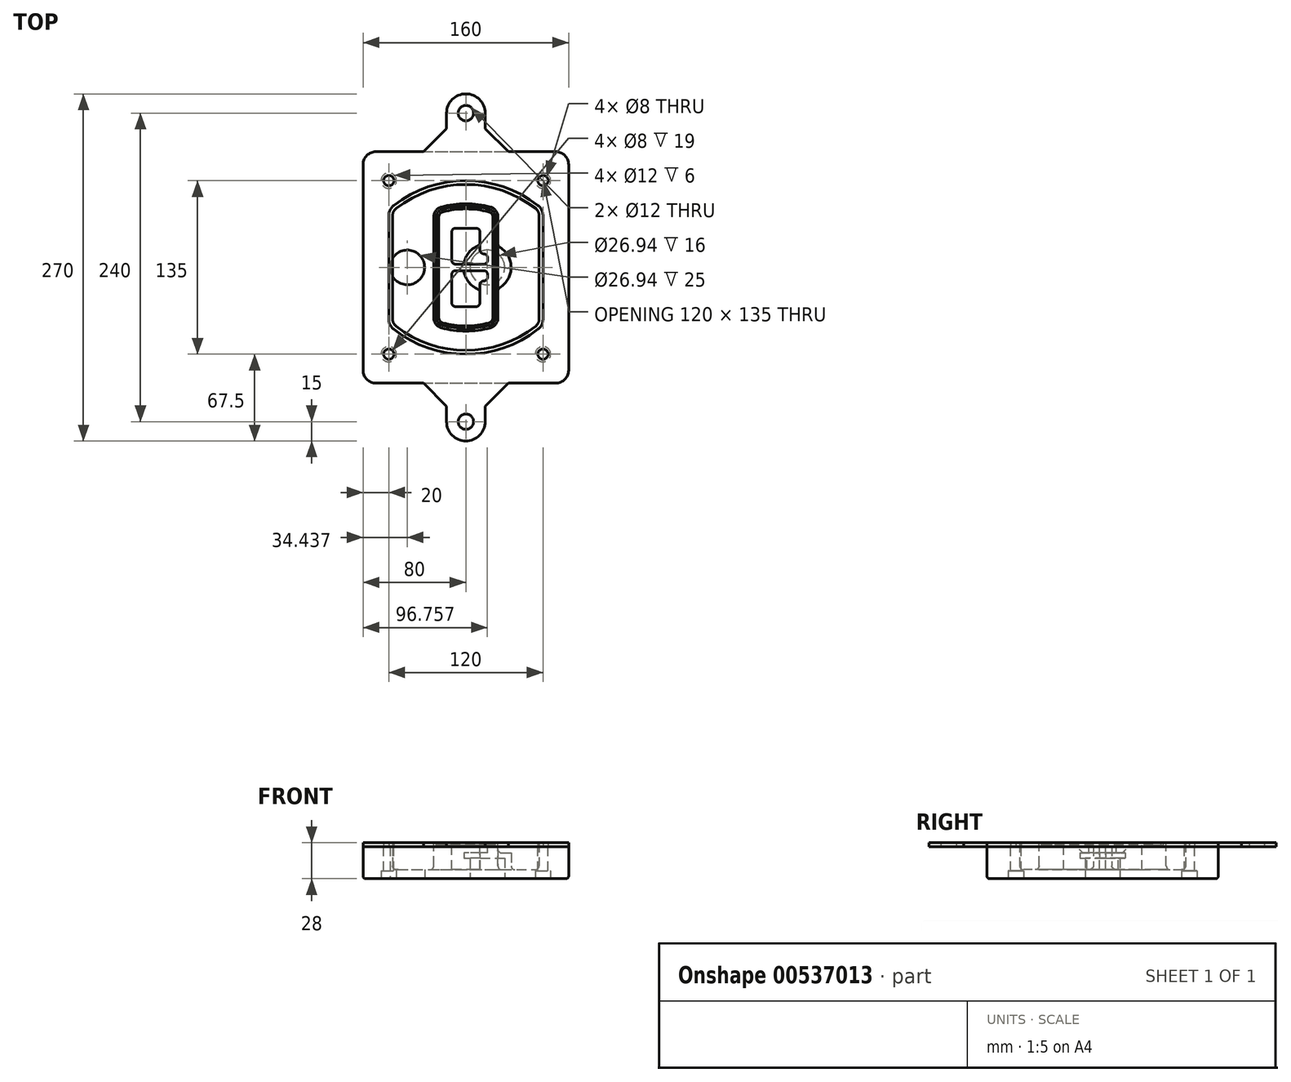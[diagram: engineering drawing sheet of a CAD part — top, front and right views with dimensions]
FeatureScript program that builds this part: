
annotation { "Feature Type Name" : "Feature", "Feature Type Description" : "" }
export const myFeature = defineFeature(function(context is Context, id is Id, definition is map)
    precondition{}
    {
        {
            var Q0;
            Q0=qCreatedBy(makeId("Top.planeOp"),FACE);
            var sketch = newSketch(context, id + "F0", { "sketchPlane" : qUnion([Q0])});
            skPoint(sketch, "E0.rect.middle", {"position": v(0, 0) * mm});
            skLineSegment(sketch, "E1.bottom", {"start": v(-70, -90) * mm, "end": v(70, -90) * mm});
            skLineSegment(sketch, "E1.top", {"start": v(-70, 90) * mm, "end": v(70, 90) * mm});
            skLineSegment(sketch, "E1.left", {"start": v(-80, -80) * mm, "end": v(-80, 80) * mm});
            skLineSegment(sketch, "E1.right", {"start": v(80, -80) * mm, "end": v(80, 80) * mm});
            skLineSegment(sketch, "E2", {"start": v(-80, 90) * mm, "end": v(80, -90) * mm, "construction": true});
            skLineSegment(sketch, "E3", {"start": v(80, 90) * mm, "end": v(-80, -90) * mm, "construction": true});
            skCircle(sketch, "E4", {"center": v(-60, 67.5) * mm, "radius": 4 * mm});
            skCircle(sketch, "E5", {"center": v(60, 67.5) * mm, "radius": 4 * mm});
            skCircle(sketch, "E6", {"center": v(60, -67.5) * mm, "radius": 4 * mm});
            skCircle(sketch, "E7", {"center": v(-60, -67.5) * mm, "radius": 4 * mm});
            skLineSegment(sketch, "E8", {"start": v(-60, 67.5) * mm, "end": v(60, 67.5) * mm, "construction": true});
            skLineSegment(sketch, "E9", {"start": v(60, 67.5) * mm, "end": v(60, -67.5) * mm, "construction": true});
            skLineSegment(sketch, "E10", {"start": v(60, -67.5) * mm, "end": v(-60, -67.5) * mm, "construction": true});
            skLineSegment(sketch, "E11", {"start": v(-60, -67.5) * mm, "end": v(-60, 67.5) * mm, "construction": true});
            skLineSegment(sketch, "E12", {"start": v(-60, 40.3) * mm, "end": v(-60, -40.3) * mm});
            skLineSegment(sketch, "E13", {"start": v(60, 40.3) * mm, "end": v(60, -40.3) * mm});
            skArc(sketch, "E14", {"start": v(56.15, 48.18) * mm, "mid": v(0, 67.5) * mm, "end": v(-56.15, 48.18) * mm});
            skArc(sketch, "E15", {"start": v(-56.15, -48.18) * mm, "mid": v(0, -67.5) * mm, "end": v(56.15, -48.18) * mm});
            skLineSegment(sketch, "E16", {"start": v(-60, 0) * mm, "end": v(60, 0) * mm, "construction": true});
            skPoint(sketch, "E17.visualSharp", {"position": v(-60, -45) * mm});
            skArc(sketch, "E17.filletArc", {"start": v(-60, -40.3) * mm, "mid": v(-58.99, -44.68) * mm, "end": v(-56.15, -48.18) * mm});
            skPoint(sketch, "E18.visualSharp", {"position": v(-60, 45) * mm});
            skArc(sketch, "E18.filletArc", {"start": v(-56.15, 48.18) * mm, "mid": v(-58.99, 44.68) * mm, "end": v(-60, 40.3) * mm});
            skPoint(sketch, "E19.visualSharp", {"position": v(60, 45) * mm});
            skArc(sketch, "E19.filletArc", {"start": v(60, 40.3) * mm, "mid": v(58.99, 44.68) * mm, "end": v(56.15, 48.18) * mm});
            skPoint(sketch, "E20.visualSharp", {"position": v(60, -45) * mm});
            skArc(sketch, "E20.filletArc", {"start": v(56.15, -48.18) * mm, "mid": v(58.99, -44.68) * mm, "end": v(60, -40.3) * mm});
            skPoint(sketch, "E21.visualSharp", {"position": v(-80, 90) * mm});
            skArc(sketch, "E21.filletArc", {"start": v(-70, 90) * mm, "mid": v(-77.07, 87.07) * mm, "end": v(-80, 80) * mm});
            skPoint(sketch, "E22.visualSharp", {"position": v(80, 90) * mm});
            skArc(sketch, "E22.filletArc", {"start": v(80, 80) * mm, "mid": v(77.07, 87.07) * mm, "end": v(70, 90) * mm});
            skPoint(sketch, "E23.visualSharp", {"position": v(80, -90) * mm});
            skArc(sketch, "E23.filletArc", {"start": v(70, -90) * mm, "mid": v(77.07, -87.07) * mm, "end": v(80, -80) * mm});
            skPoint(sketch, "E24.visualSharp", {"position": v(-80, -90) * mm});
            skArc(sketch, "E24.filletArc", {"start": v(-80, -80) * mm, "mid": v(-77.07, -87.07) * mm, "end": v(-70, -90) * mm});
            skArc(sketch, "E25.0", {"start": v(57, 40.3) * mm, "mid": v(56.3, 43.36) * mm, "end": v(54.3, 45.81) * mm});
            skLineSegment(sketch, "E25.1", {"start": v(57, 40.3) * mm, "end": v(57, -40.3) * mm});
            skArc(sketch, "E25.2", {"start": v(54.3, -45.81) * mm, "mid": v(56.3, -43.36) * mm, "end": v(57, -40.3) * mm});
            skArc(sketch, "E25.3", {"start": v(-54.3, -45.81) * mm, "mid": v(0, -64.5) * mm, "end": v(54.3, -45.81) * mm});
            skArc(sketch, "E25.4", {"start": v(-57, -40.3) * mm, "mid": v(-56.3, -43.36) * mm, "end": v(-54.3, -45.81) * mm});
            skArc(sketch, "E25.5", {"start": v(54.3, 45.81) * mm, "mid": v(0, 64.5) * mm, "end": v(-54.3, 45.81) * mm});
            skLineSegment(sketch, "E25.6", {"start": v(-57, 40.3) * mm, "end": v(-57, -40.3) * mm});
            skArc(sketch, "E25.7", {"start": v(-54.3, 45.81) * mm, "mid": v(-56.3, 43.36) * mm, "end": v(-57, 40.3) * mm});
            skArc(sketch, "E26.0", {"start": v(-58.62, 51.33) * mm, "mid": v(-62.58, 46.43) * mm, "end": v(-64, 40.3) * mm});
            skArc(sketch, "E26.1", {"start": v(58.62, 51.33) * mm, "mid": v(0, 71.5) * mm, "end": v(-58.62, 51.33) * mm});
            skArc(sketch, "E26.2", {"start": v(64, 40.3) * mm, "mid": v(62.58, 46.43) * mm, "end": v(58.62, 51.33) * mm});
            skLineSegment(sketch, "E26.3", {"start": v(64, 40.3) * mm, "end": v(64, -40.3) * mm});
            skArc(sketch, "E26.4", {"start": v(58.62, -51.33) * mm, "mid": v(62.58, -46.43) * mm, "end": v(64, -40.3) * mm});
            skLineSegment(sketch, "E26.5", {"start": v(-64, 40.3) * mm, "end": v(-64, -40.3) * mm});
            skArc(sketch, "E26.6", {"start": v(-58.62, -51.33) * mm, "mid": v(0, -71.5) * mm, "end": v(58.62, -51.33) * mm});
            skArc(sketch, "E26.7", {"start": v(-64, -40.3) * mm, "mid": v(-62.58, -46.43) * mm, "end": v(-58.62, -51.33) * mm});
            skSolve(sketch);
        }
        {
            var Q0;
            Q0=makeQuery(id+"F0.imprint","IMPRINT",FACE,{"disambiguationData":[TD([[makeQuery(id+"F0.imprint","IMPRINT",EDGE,{"derivedFrom":sQuery(id+"F0.wireOp",EDGE,"E1.bottom")}),1.0]])]});
            var Q1;
            Q1=makeQuery(id+"F0.imprint","IMPRINT",FACE,{"disambiguationData":[TD([[makeQuery(id+"F0.imprint","IMPRINT",EDGE,{"derivedFrom":sQuery(id+"F0.wireOp",EDGE,"E12")}),1.0]])]});
            var Q2;
            Q2=makeQuery(id+"F0.imprint","IMPRINT",FACE,{"disambiguationData":[TD([[makeQuery(id+"F0.imprint","IMPRINT",EDGE,{"derivedFrom":sQuery(id+"F0.wireOp",EDGE,"E25.0")}),1.0]])]});
            var Q3;
            Q3=makeQuery(id+"F0.imprint","IMPRINT",FACE,{"disambiguationData":[TD([[makeQuery(id+"F0.imprint","IMPRINT",EDGE,{"derivedFrom":sQuery(id+"F0.wireOp",EDGE,"E12")}),-1.0]])]});
            extrude(context, id + "F1", {"entities" : qUnion([Q0, Q1, Q2, Q3]), "oppositeDirection" : true, "depth" : 25 * mm});
        }
        {
            var Q0;
            Q0=makeQuery(id+"F0.imprint","IMPRINT",FACE,{"disambiguationData":[TD([[makeQuery(id+"F0.imprint","IMPRINT",EDGE,{"derivedFrom":sQuery(id+"F0.wireOp",EDGE,"E12")}),1.0]])]});
            extrude(context, id + "F2", {"entities" : qUnion([Q0]), "operationType" : NewBodyOperationType.ADD, "depth" : 3 * mm});
        }
        {
            var Q0;
            Q0=makeQuery(id+"F0.imprint","IMPRINT",FACE,{"disambiguationData":[TD([[makeQuery(id+"F0.imprint","IMPRINT",EDGE,{"derivedFrom":sQuery(id+"F0.wireOp",EDGE,"E25.0")}),1.0]])]});
            extrude(context, id + "F3", {"entities" : qUnion([Q0]), "operationType" : NewBodyOperationType.REMOVE, "oppositeDirection" : true, "depth" : 18 * mm});
        }
        {
            var Q0;
            Q0=makeQuery(id+"F2.opExtrude","CAP_FACE",FACE,{"disambiguationData":[OSD([sQuery(id+"F0.wireOp",EDGE,"E12"),sQuery(id+"F0.wireOp",EDGE,"E13"),sQuery(id+"F0.wireOp",EDGE,"E14"),sQuery(id+"F0.wireOp",EDGE,"E15"),sQuery(id+"F0.wireOp",EDGE,"E17.filletArc"),sQuery(id+"F0.wireOp",EDGE,"E18.filletArc"),sQuery(id+"F0.wireOp",EDGE,"E19.filletArc"),sQuery(id+"F0.wireOp",EDGE,"E20.filletArc"),sQuery(id+"F0.wireOp",EDGE,"E25.0"),sQuery(id+"F0.wireOp",EDGE,"E25.1"),sQuery(id+"F0.wireOp",EDGE,"E25.2"),sQuery(id+"F0.wireOp",EDGE,"E25.3"),sQuery(id+"F0.wireOp",EDGE,"E25.4"),sQuery(id+"F0.wireOp",EDGE,"E25.5"),sQuery(id+"F0.wireOp",EDGE,"E25.6"),sQuery(id+"F0.wireOp",EDGE,"E25.7")])],"isStart":false});
            var sketch = newSketch(context, id + "F4", { "sketchPlane" : qUnion([Q0])});
            skArc(sketch, "E27.0", {"start": v(-19.08, -46.97) * mm, "mid": v(0, -49.5) * mm, "end": v(19.08, -46.97) * mm});
            skArc(sketch, "E28.0", {"start": v(19.08, 46.97) * mm, "mid": v(0, 49.5) * mm, "end": v(-19.08, 46.97) * mm});
            skLineSegment(sketch, "E29", {"start": v(-25, 39.25) * mm, "end": v(-25, -39.25) * mm});
            skLineSegment(sketch, "E30", {"start": v(25, 39.25) * mm, "end": v(25, -39.25) * mm});
            skLineSegment(sketch, "E31", {"start": v(-25, 45.1) * mm, "end": v(25, 45.1) * mm, "construction": true});
            skLineSegment(sketch, "E32", {"start": v(-25, -45.1) * mm, "end": v(25, -45.1) * mm, "construction": true});
            skPoint(sketch, "E33.visualSharp", {"position": v(-25, 45.1) * mm});
            skArc(sketch, "E33.filletArc", {"start": v(-19.08, 46.97) * mm, "mid": v(-23.35, 44.11) * mm, "end": v(-25, 39.25) * mm});
            skPoint(sketch, "E34.visualSharp", {"position": v(25, 45.1) * mm});
            skArc(sketch, "E34.filletArc", {"start": v(25, 39.25) * mm, "mid": v(23.35, 44.11) * mm, "end": v(19.08, 46.97) * mm});
            skPoint(sketch, "E35.visualSharp", {"position": v(25, -45.1) * mm});
            skArc(sketch, "E35.filletArc", {"start": v(19.08, -46.97) * mm, "mid": v(23.35, -44.11) * mm, "end": v(25, -39.25) * mm});
            skPoint(sketch, "E36.visualSharp", {"position": v(-25, -45.1) * mm});
            skArc(sketch, "E36.filletArc", {"start": v(-25, -39.25) * mm, "mid": v(-23.35, -44.11) * mm, "end": v(-19.08, -46.97) * mm});
            skArc(sketch, "E37.0", {"start": v(54.3, 45.81) * mm, "mid": v(0, 64.5) * mm, "end": v(-54.3, 45.81) * mm});
            skArc(sketch, "E37.1", {"start": v(-54.3, 45.81) * mm, "mid": v(-56.3, 43.36) * mm, "end": v(-57, 40.3) * mm});
            skLineSegment(sketch, "E37.2", {"start": v(-57, 40.3) * mm, "end": v(-57, -40.3) * mm});
            skArc(sketch, "E37.3", {"start": v(-57, -40.3) * mm, "mid": v(-56.3, -43.36) * mm, "end": v(-54.3, -45.81) * mm});
            skArc(sketch, "E37.4", {"start": v(-54.3, -45.81) * mm, "mid": v(0, -64.5) * mm, "end": v(54.3, -45.81) * mm});
            skArc(sketch, "E37.5", {"start": v(54.3, -45.81) * mm, "mid": v(56.3, -43.36) * mm, "end": v(57, -40.3) * mm});
            skLineSegment(sketch, "E37.6", {"start": v(57, 40.3) * mm, "end": v(57, -40.3) * mm});
            skArc(sketch, "E37.7", {"start": v(57, 40.3) * mm, "mid": v(56.3, 43.36) * mm, "end": v(54.3, 45.81) * mm});
            skLineSegment(sketch, "E38.0", {"start": v(23, 39.25) * mm, "end": v(23, -39.25) * mm});
            skArc(sketch, "E38.1", {"start": v(18.56, -45.04) * mm, "mid": v(21.76, -42.9) * mm, "end": v(23, -39.25) * mm});
            skArc(sketch, "E38.2", {"start": v(-18.56, -45.04) * mm, "mid": v(0, -47.5) * mm, "end": v(18.56, -45.04) * mm});
            skArc(sketch, "E38.3", {"start": v(-23, -39.25) * mm, "mid": v(-21.76, -42.9) * mm, "end": v(-18.56, -45.04) * mm});
            skLineSegment(sketch, "E38.4", {"start": v(-23, 39.25) * mm, "end": v(-23, -39.25) * mm});
            skArc(sketch, "E38.5", {"start": v(23, 39.25) * mm, "mid": v(21.76, 42.9) * mm, "end": v(18.56, 45.04) * mm});
            skArc(sketch, "E38.6", {"start": v(-18.56, 45.04) * mm, "mid": v(-21.76, 42.9) * mm, "end": v(-23, 39.25) * mm});
            skArc(sketch, "E38.7", {"start": v(18.56, 45.04) * mm, "mid": v(0, 47.5) * mm, "end": v(-18.56, 45.04) * mm});
            skArc(sketch, "E39.0", {"start": v(21, 39.25) * mm, "mid": v(20.18, 41.68) * mm, "end": v(18.04, 43.1) * mm});
            skLineSegment(sketch, "E39.1", {"start": v(21, 39.25) * mm, "end": v(21, -39.25) * mm});
            skArc(sketch, "E39.2", {"start": v(18.04, -43.1) * mm, "mid": v(20.18, -41.68) * mm, "end": v(21, -39.25) * mm});
            skArc(sketch, "E39.3", {"start": v(-18.04, -43.1) * mm, "mid": v(0, -45.5) * mm, "end": v(18.04, -43.1) * mm});
            skArc(sketch, "E39.4", {"start": v(-21, -39.25) * mm, "mid": v(-20.18, -41.68) * mm, "end": v(-18.04, -43.1) * mm});
            skArc(sketch, "E39.5", {"start": v(18.04, 43.1) * mm, "mid": v(0, 45.5) * mm, "end": v(-18.04, 43.1) * mm});
            skLineSegment(sketch, "E39.6", {"start": v(-21, 39.25) * mm, "end": v(-21, -39.25) * mm});
            skArc(sketch, "E39.7", {"start": v(-18.04, 43.1) * mm, "mid": v(-20.18, 41.68) * mm, "end": v(-21, 39.25) * mm});
            skLineSegment(sketch, "E40", {"start": v(-25, 0) * mm, "end": v(25, 0) * mm, "construction": true});
            skLineSegment(sketch, "E41", {"start": v(-11, 5.5) * mm, "end": v(-11, 27.5) * mm});
            skLineSegment(sketch, "E42", {"start": v(-8, 30.5) * mm, "end": v(8, 30.5) * mm});
            skLineSegment(sketch, "E43", {"start": v(11, 27.5) * mm, "end": v(11, 13.5) * mm});
            skLineSegment(sketch, "E44", {"start": v(14, 10.5) * mm, "end": v(14, 10.5) * mm});
            skLineSegment(sketch, "E45", {"start": v(17, 7.5) * mm, "end": v(17, 5.5) * mm});
            skLineSegment(sketch, "E46", {"start": v(14, 2.5) * mm, "end": v(-8, 2.5) * mm});
            skPoint(sketch, "E47.visualSharp", {"position": v(-11, 30.5) * mm});
            skArc(sketch, "E47.filletArc", {"start": v(-8, 30.5) * mm, "mid": v(-10.12, 29.62) * mm, "end": v(-11, 27.5) * mm});
            skPoint(sketch, "E48.visualSharp", {"position": v(11, 30.5) * mm});
            skArc(sketch, "E48.filletArc", {"start": v(11, 27.5) * mm, "mid": v(10.12, 29.62) * mm, "end": v(8, 30.5) * mm});
            skPoint(sketch, "E49.visualSharp", {"position": v(11, 10.5) * mm});
            skArc(sketch, "E49.filletArc", {"start": v(11, 13.5) * mm, "mid": v(11.88, 11.38) * mm, "end": v(14, 10.5) * mm});
            skPoint(sketch, "E50.visualSharp", {"position": v(17, 10.5) * mm});
            skArc(sketch, "E50.filletArc", {"start": v(17, 7.5) * mm, "mid": v(16.12, 9.62) * mm, "end": v(14, 10.5) * mm});
            skPoint(sketch, "E51.visualSharp", {"position": v(17, 2.5) * mm});
            skArc(sketch, "E51.filletArc", {"start": v(14, 2.5) * mm, "mid": v(16.12, 3.38) * mm, "end": v(17, 5.5) * mm});
            skPoint(sketch, "E52.visualSharp", {"position": v(-11, 2.5) * mm});
            skArc(sketch, "E52.filletArc", {"start": v(-11, 5.5) * mm, "mid": v(-10.12, 3.38) * mm, "end": v(-8, 2.5) * mm});
            skLineSegment(sketch, "E53.0.MirrorCS", {"start": v(14, -2.5) * mm, "end": v(-8, -2.5) * mm});
            skArc(sketch, "E54.0.MirrorCS", {"start": v(-11, -5.5) * mm, "mid": v(-10.12, -3.38) * mm, "end": v(-8, -2.5) * mm});
            skLineSegment(sketch, "E55.0.MirrorCS", {"start": v(-11, -5.5) * mm, "end": v(-11, -27.5) * mm});
            skArc(sketch, "E56.0.MirrorCS", {"start": v(-8, -30.5) * mm, "mid": v(-10.12, -29.62) * mm, "end": v(-11, -27.5) * mm});
            skLineSegment(sketch, "E57.0.MirrorCS", {"start": v(-8, -30.5) * mm, "end": v(8, -30.5) * mm});
            skArc(sketch, "E58.0.MirrorCS", {"start": v(11, -27.5) * mm, "mid": v(10.12, -29.62) * mm, "end": v(8, -30.5) * mm});
            skLineSegment(sketch, "E59.0.MirrorCS", {"start": v(11, -27.5) * mm, "end": v(11, -13.5) * mm});
            skArc(sketch, "E60.0.MirrorCS", {"start": v(11, -13.5) * mm, "mid": v(11.88, -11.38) * mm, "end": v(14, -10.5) * mm});
            skArc(sketch, "E61.0.MirrorCS", {"start": v(17, -7.5) * mm, "mid": v(16.12, -9.62) * mm, "end": v(14, -10.5) * mm});
            skLineSegment(sketch, "E62.0.MirrorCS", {"start": v(17, -7.5) * mm, "end": v(17, -5.5) * mm});
            skArc(sketch, "E63.0.MirrorCS", {"start": v(14, -2.5) * mm, "mid": v(16.12, -3.38) * mm, "end": v(17, -5.5) * mm});
            skSolve(sketch);
        }
        {
            var Q0;
            Q0=makeQuery(id+"F4.imprint","IMPRINT",FACE,{"disambiguationData":[TD([[makeQuery(id+"F4.imprint","IMPRINT",EDGE,{"derivedFrom":sQuery(id+"F4.wireOp",EDGE,"E27.0")}),1.0]])]});
            var Q1;
            Q1=makeQuery(id+"F4.imprint","IMPRINT",FACE,{"disambiguationData":[TD([[makeQuery(id+"F4.imprint","IMPRINT",EDGE,{"derivedFrom":sQuery(id+"F4.wireOp",EDGE,"E38.0")}),-1.0]])]});
            var Q2;
            Q2=makeQuery(id+"F4.imprint","IMPRINT",FACE,{"disambiguationData":[TD([[makeQuery(id+"F4.imprint","IMPRINT",EDGE,{"derivedFrom":sQuery(id+"F4.wireOp",EDGE,"E39.0")}),1.0]])]});
            extrude(context, id + "F5", {"entities" : qUnion([Q0, Q1, Q2]), "operationType" : NewBodyOperationType.ADD, "endBound" : BoundingType.UP_TO_NEXT, "oppositeDirection" : true, "depth" : 25 * mm});
        }
        {
            var Q0;
            Q0=makeQuery(id+"F4.imprint","IMPRINT",FACE,{"disambiguationData":[TD([[makeQuery(id+"F4.imprint","IMPRINT",EDGE,{"derivedFrom":sQuery(id+"F4.wireOp",EDGE,"E38.0")}),-1.0]])]});
            extrude(context, id + "F6", {"entities" : qUnion([Q0]), "operationType" : NewBodyOperationType.REMOVE, "oppositeDirection" : true, "depth" : 2 * mm});
        }
        {
            var Q0;
            Q0=makeQuery(id+"F1.opExtrude","CAP_FACE",FACE,{"disambiguationData":[OSD([sQuery(id+"F0.wireOp",EDGE,"E1.bottom"),sQuery(id+"F0.wireOp",EDGE,"E1.top"),sQuery(id+"F0.wireOp",EDGE,"E1.left"),sQuery(id+"F0.wireOp",EDGE,"E1.right"),sQuery(id+"F0.wireOp",EDGE,"E4"),sQuery(id+"F0.wireOp",EDGE,"E5"),sQuery(id+"F0.wireOp",EDGE,"E6"),sQuery(id+"F0.wireOp",EDGE,"E7"),sQuery(id+"F0.wireOp",EDGE,"E21.filletArc"),sQuery(id+"F0.wireOp",EDGE,"E22.filletArc"),sQuery(id+"F0.wireOp",EDGE,"E23.filletArc"),sQuery(id+"F0.wireOp",EDGE,"E24.filletArc")])],"isStart":false});
            var sketch = newSketch(context, id + "F7", { "sketchPlane" : qUnion([Q0])});
            skCircle(sketch, "E64", {"center": v(16.76, 0) * mm, "radius": 13.47 * mm});
            skCircle(sketch, "E65", {"center": v(-45.56, 0) * mm, "radius": 13.47 * mm});
            skLineSegment(sketch, "E66", {"start": v(80, 0) * mm, "end": v(-80, 0) * mm});
            skCircle(sketch, "E67", {"center": v(16.76, 0) * mm, "radius": 18.47 * mm});
            skCircle(sketch, "E68", {"center": v(60, -67.5) * mm, "radius": 6 * mm});
            skCircle(sketch, "E69", {"center": v(-60, -67.5) * mm, "radius": 6 * mm});
            skCircle(sketch, "E70", {"center": v(-60, 67.5) * mm, "radius": 6 * mm});
            skCircle(sketch, "E71", {"center": v(60, 67.5) * mm, "radius": 6 * mm});
            skSolve(sketch);
        }
        {
            var Q0;
            {var subQ1=sQuery(id+"F7.wireOp",EDGE,"E66");var subQ4=sQuery(id+"F7.wireOp",EDGE,"E64");var subQ6=makeQuery(id+"F7.imprint","INTERSECT",VERTEX,{"disambiguationData":[OD(0.0)],"derivedFrom":[subQ4,subQ1]});Q0=makeQuery(id+"F7.imprint","IMPRINT",FACE,{"disambiguationData":[TD([[makeQuery(id+"F7.imprint","IMPRINT",EDGE,{"disambiguationData":[TD([[subQ6,-1.0]])],"derivedFrom":subQ4}),-1.0]])]});}
            var Q1;
            {var subQ0=sQuery(id+"F7.wireOp",EDGE,"E66");var subQ1=sQuery(id+"F7.wireOp",EDGE,"E64");var subQ3=makeQuery(id+"F7.imprint","INTERSECT",VERTEX,{"disambiguationData":[OD(0.0)],"derivedFrom":[subQ1,subQ0]});Q1=makeQuery(id+"F7.imprint","IMPRINT",FACE,{"disambiguationData":[TD([[makeQuery(id+"F7.imprint","IMPRINT",EDGE,{"disambiguationData":[TD([[subQ3,-1.0]])],"derivedFrom":subQ1}),1.0]])]});}
            var Q2;
            {var subQ0=sQuery(id+"F7.wireOp",EDGE,"E66");var subQ1=sQuery(id+"F7.wireOp",EDGE,"E64");var subQ3=makeQuery(id+"F7.imprint","INTERSECT",VERTEX,{"disambiguationData":[OD(0.0)],"derivedFrom":[subQ1,subQ0]});Q2=makeQuery(id+"F7.imprint","IMPRINT",FACE,{"disambiguationData":[TD([[makeQuery(id+"F7.imprint","IMPRINT",EDGE,{"disambiguationData":[TD([[subQ3,1.0]])],"derivedFrom":subQ1}),1.0]])]});}
            var Q3;
            {var subQ1=sQuery(id+"F7.wireOp",EDGE,"E66");var subQ4=sQuery(id+"F7.wireOp",EDGE,"E64");var subQ6=makeQuery(id+"F7.imprint","INTERSECT",VERTEX,{"disambiguationData":[OD(0.0)],"derivedFrom":[subQ4,subQ1]});Q3=makeQuery(id+"F7.imprint","IMPRINT",FACE,{"disambiguationData":[TD([[makeQuery(id+"F7.imprint","IMPRINT",EDGE,{"disambiguationData":[TD([[subQ6,1.0]])],"derivedFrom":subQ4}),-1.0]])]});}
            extrude(context, id + "F8", {"entities" : qUnion([Q0, Q1, Q2, Q3]), "operationType" : NewBodyOperationType.ADD, "oppositeDirection" : true, "depth" : 20 * mm});
        }
        {
            var Q0;
            {var subQ0=sQuery(id+"F7.wireOp",EDGE,"E66");var subQ1=sQuery(id+"F7.wireOp",EDGE,"E64");var subQ3=makeQuery(id+"F7.imprint","INTERSECT",VERTEX,{"disambiguationData":[OD(0.0)],"derivedFrom":[subQ1,subQ0]});Q0=makeQuery(id+"F7.imprint","IMPRINT",FACE,{"disambiguationData":[TD([[makeQuery(id+"F7.imprint","IMPRINT",EDGE,{"disambiguationData":[TD([[subQ3,-1.0]])],"derivedFrom":subQ1}),1.0]])]});}
            var Q1;
            {var subQ0=sQuery(id+"F7.wireOp",EDGE,"E66");var subQ1=sQuery(id+"F7.wireOp",EDGE,"E64");var subQ3=makeQuery(id+"F7.imprint","INTERSECT",VERTEX,{"disambiguationData":[OD(0.0)],"derivedFrom":[subQ1,subQ0]});Q1=makeQuery(id+"F7.imprint","IMPRINT",FACE,{"disambiguationData":[TD([[makeQuery(id+"F7.imprint","IMPRINT",EDGE,{"disambiguationData":[TD([[subQ3,1.0]])],"derivedFrom":subQ1}),1.0]])]});}
            extrude(context, id + "F9", {"entities" : qUnion([Q0, Q1]), "operationType" : NewBodyOperationType.REMOVE, "oppositeDirection" : true, "depth" : 16 * mm});
        }
        {
            var Q0;
            {var subQ0=sQuery(id+"F7.wireOp",EDGE,"E66");var subQ1=sQuery(id+"F7.wireOp",EDGE,"E65");var subQ3=makeQuery(id+"F7.imprint","INTERSECT",VERTEX,{"disambiguationData":[OD(0.0)],"derivedFrom":[subQ1,subQ0]});Q0=makeQuery(id+"F7.imprint","IMPRINT",FACE,{"disambiguationData":[TD([[makeQuery(id+"F7.imprint","IMPRINT",EDGE,{"disambiguationData":[TD([[subQ3,-1.0]])],"derivedFrom":subQ1}),1.0]])]});}
            var Q1;
            {var subQ0=sQuery(id+"F7.wireOp",EDGE,"E66");var subQ1=sQuery(id+"F7.wireOp",EDGE,"E65");var subQ3=makeQuery(id+"F7.imprint","INTERSECT",VERTEX,{"disambiguationData":[OD(0.0)],"derivedFrom":[subQ1,subQ0]});Q1=makeQuery(id+"F7.imprint","IMPRINT",FACE,{"disambiguationData":[TD([[makeQuery(id+"F7.imprint","IMPRINT",EDGE,{"disambiguationData":[TD([[subQ3,1.0]])],"derivedFrom":subQ1}),1.0]])]});}
            extrude(context, id + "F10", {"entities" : qUnion([Q0, Q1]), "operationType" : NewBodyOperationType.REMOVE, "oppositeDirection" : true, "depth" : 25 * mm});
        }
        {
            var Q0;
            Q0=makeQuery(id+"F7.imprint","IMPRINT",FACE,{"disambiguationData":[TD([[makeQuery(id+"F7.imprint","IMPRINT",EDGE,{"derivedFrom":sQuery(id+"F7.wireOp",EDGE,"E68")}),1.0]])]});
            var Q1;
            Q1=makeQuery(id+"F7.imprint","IMPRINT",FACE,{"disambiguationData":[TD([[makeQuery(id+"F7.imprint","IMPRINT",EDGE,{"derivedFrom":makeQuery(id+"F1.opExtrude","CAP_EDGE",EDGE,{"disambiguationData":[OSD([sQuery(id+"F0.wireOp",EDGE,"E5")])],"isStart":false})}),-1.0]])]});
            var Q2;
            Q2=makeQuery(id+"F7.imprint","IMPRINT",FACE,{"disambiguationData":[TD([[makeQuery(id+"F7.imprint","IMPRINT",EDGE,{"derivedFrom":sQuery(id+"F7.wireOp",EDGE,"E69")}),1.0]])]});
            var Q3;
            Q3=makeQuery(id+"F7.imprint","IMPRINT",FACE,{"disambiguationData":[TD([[makeQuery(id+"F7.imprint","IMPRINT",EDGE,{"derivedFrom":makeQuery(id+"F1.opExtrude","CAP_EDGE",EDGE,{"disambiguationData":[OSD([sQuery(id+"F0.wireOp",EDGE,"E4")])],"isStart":false})}),-1.0]])]});
            var Q4;
            Q4=makeQuery(id+"F7.imprint","IMPRINT",FACE,{"disambiguationData":[TD([[makeQuery(id+"F7.imprint","IMPRINT",EDGE,{"derivedFrom":sQuery(id+"F7.wireOp",EDGE,"E70")}),1.0]])]});
            var Q5;
            Q5=makeQuery(id+"F7.imprint","IMPRINT",FACE,{"disambiguationData":[TD([[makeQuery(id+"F7.imprint","IMPRINT",EDGE,{"derivedFrom":makeQuery(id+"F1.opExtrude","CAP_EDGE",EDGE,{"disambiguationData":[OSD([sQuery(id+"F0.wireOp",EDGE,"E7")])],"isStart":false})}),-1.0]])]});
            var Q6;
            Q6=makeQuery(id+"F7.imprint","IMPRINT",FACE,{"disambiguationData":[TD([[makeQuery(id+"F7.imprint","IMPRINT",EDGE,{"derivedFrom":sQuery(id+"F7.wireOp",EDGE,"E71")}),1.0]])]});
            var Q7;
            Q7=makeQuery(id+"F7.imprint","IMPRINT",FACE,{"disambiguationData":[TD([[makeQuery(id+"F7.imprint","IMPRINT",EDGE,{"derivedFrom":makeQuery(id+"F1.opExtrude","CAP_EDGE",EDGE,{"disambiguationData":[OSD([sQuery(id+"F0.wireOp",EDGE,"E6")])],"isStart":false})}),-1.0]])]});
            extrude(context, id + "F11", {"entities" : qUnion([Q0, Q1, Q2, Q3, Q4, Q5, Q6, Q7]), "operationType" : NewBodyOperationType.REMOVE, "oppositeDirection" : true, "depth" : 6 * mm});
        }
        {
            var Q0;
            Q0=makeQuery(id+"F9.boolean.opBoolean","COPY",FACE,{"derivedFrom":makeQuery(id+"F9.opExtrude","CAP_FACE",FACE,{"disambiguationData":[OSD([sQuery(id+"F7.wireOp",EDGE,"E64")])],"isStart":false})});
            var sketch = newSketch(context, id + "F12", { "sketchPlane" : qUnion([Q0])});
            skArc(sketch, "E72.0", {"start": v(11, 17.55) * mm, "mid": v(2.57, 11.82) * mm, "end": v(-1.54, 2.5) * mm});
            skArc(sketch, "E72.1", {"start": v(-1.54, -2.5) * mm, "mid": v(2.57, -11.82) * mm, "end": v(11, -17.55) * mm});
            skLineSegment(sketch, "E73", {"start": v(-1.54, -2.5) * mm, "end": v(14, -2.5) * mm});
            skLineSegment(sketch, "E74.0", {"start": v(14, 2.5) * mm, "end": v(-1.54, 2.5) * mm});
            skArc(sketch, "E74.1", {"start": v(14, 2.5) * mm, "mid": v(16.12, 3.38) * mm, "end": v(17, 5.5) * mm});
            skLineSegment(sketch, "E74.2", {"start": v(17, 7.5) * mm, "end": v(17, 5.5) * mm});
            skArc(sketch, "E74.3", {"start": v(17, 7.5) * mm, "mid": v(16.12, 9.62) * mm, "end": v(14, 10.5) * mm});
            skArc(sketch, "E74.4", {"start": v(11, 13.5) * mm, "mid": v(11.88, 11.38) * mm, "end": v(14, 10.5) * mm});
            skLineSegment(sketch, "E74.5", {"start": v(11, 17.55) * mm, "end": v(11, 13.5) * mm});
            skLineSegment(sketch, "E74.7", {"start": v(14, -2.5) * mm, "end": v(-1.54, -2.5) * mm});
            skArc(sketch, "E74.8", {"start": v(14, -2.5) * mm, "mid": v(16.12, -3.38) * mm, "end": v(17, -5.5) * mm});
            skLineSegment(sketch, "E74.9", {"start": v(17, -7.5) * mm, "end": v(17, -5.5) * mm});
            skArc(sketch, "E74.10", {"start": v(17, -7.5) * mm, "mid": v(16.12, -9.62) * mm, "end": v(14, -10.5) * mm});
            skArc(sketch, "E74.11", {"start": v(11, -13.5) * mm, "mid": v(11.88, -11.38) * mm, "end": v(14, -10.5) * mm});
            skLineSegment(sketch, "E74.12", {"start": v(11, -17.55) * mm, "end": v(11, -13.5) * mm});
            skPoint(sketch, "E75.orphan", {"position": v(11, -27.5) * mm});
            skPoint(sketch, "E76.orphan", {"position": v(-8, -2.5) * mm});
            skPoint(sketch, "E77.orphan", {"position": v(-8, 2.5) * mm});
            skPoint(sketch, "E78.orphan", {"position": v(11, 27.5) * mm});
            skSolve(sketch);
        }
        {
            var Q0;
            {var subQ7=sQuery(id+"F12.wireOp",EDGE,"E72.0");var subQ14=sQuery(id+"F12.wireOp",EDGE,"E72.1");var subQ16=sQuery(id+"F12.wireOp",EDGE,"E74.1");var subQ18=sQuery(id+"F12.wireOp",EDGE,"E74.8");Q0=qUnion([makeQuery(id+"F12.imprint","IMPRINT",FACE,{"disambiguationData":[TD([[makeQuery(id+"F12.imprint","IMPRINT",EDGE,{"derivedFrom":subQ7}),1.0]])]}),makeQuery(id+"F12.imprint","IMPRINT",FACE,{"disambiguationData":[TD([[makeQuery(id+"F12.imprint","IMPRINT",EDGE,{"derivedFrom":subQ14}),1.0]])]}),makeQuery(id+"F12.imprint","IMPRINT",FACE,{"disambiguationData":[TD([[makeQuery(id+"F12.imprint","IMPRINT",EDGE,{"derivedFrom":subQ16}),1.0]])]}),makeQuery(id+"F12.imprint","IMPRINT",FACE,{"disambiguationData":[TD([[makeQuery(id+"F12.imprint","IMPRINT",EDGE,{"derivedFrom":subQ18}),-1.0]])]})]);}
            var Q1;
            Q1=makeQuery(id+"F5.boolean.opBoolean","SPLIT",FACE,{"disambiguationData":[TD([makeQuery(id+"F5.opExtrude","SWEPT_FACE",FACE,{"disambiguationData":[OSD([sQuery(id+"F4.wireOp",EDGE,"E41")])]})])],"derivedFrom":makeQuery(id+"F3.boolean.opBoolean","COPY",FACE,{"derivedFrom":makeQuery(id+"F3.opExtrude","CAP_FACE",FACE,{"disambiguationData":[OSD([sQuery(id+"F0.wireOp",EDGE,"E25.0"),sQuery(id+"F0.wireOp",EDGE,"E25.1"),sQuery(id+"F0.wireOp",EDGE,"E25.2"),sQuery(id+"F0.wireOp",EDGE,"E25.3"),sQuery(id+"F0.wireOp",EDGE,"E25.4"),sQuery(id+"F0.wireOp",EDGE,"E25.5"),sQuery(id+"F0.wireOp",EDGE,"E25.6"),sQuery(id+"F0.wireOp",EDGE,"E25.7")])],"isStart":false})})});
            extrude(context, id + "F13", {"entities" : qUnion([Q0]), "operationType" : NewBodyOperationType.REMOVE, "endBound" : BoundingType.UP_TO_SURFACE, "endBoundEntityFace" : qUnion([Q1]), "depth" : 25 * mm});
        }
        {
            var Q0;
            Q0=makeQuery(id+"F3.boolean.opBoolean","COPY",EDGE,{"derivedFrom":makeQuery(id+"F3.opExtrude","CAP_EDGE",EDGE,{"disambiguationData":[OSD([sQuery(id+"F0.wireOp",EDGE,"E25.6")])],"isStart":false})});
            var Q1;
            Q1=makeQuery(id+"F8.boolean.opBoolean","INTERSECT",EDGE,{"derivedFrom":[makeQuery(id+"F5.opExtrude","SWEPT_FACE",FACE,{"disambiguationData":[OSD([sQuery(id+"F4.wireOp",EDGE,"E30")])]}),makeQuery(id+"F8.opExtrude","CAP_FACE",FACE,{"disambiguationData":[OSD([sQuery(id+"F7.wireOp",EDGE,"E67")])],"isStart":false})]});
            var Q2;
            Q2=makeQuery(id+"F8.boolean.opBoolean","INTERSECT",EDGE,{"disambiguationData":[OD(1.0)],"derivedFrom":[makeQuery(id+"F5.opExtrude","SWEPT_FACE",FACE,{"disambiguationData":[OSD([sQuery(id+"F4.wireOp",EDGE,"E30")])]}),makeQuery(id+"F8.opExtrude","SWEPT_FACE",FACE,{"disambiguationData":[OSD([sQuery(id+"F7.wireOp",EDGE,"E67")])]})]});
            var Q3;
            {var subQ0=sQuery(id+"F4.wireOp",EDGE,"E30");Q3=makeQuery(id+"F8.boolean.opBoolean","SPLIT",EDGE,{"disambiguationData":[TD([makeQuery(id+"F5.opExtrude","SWEPT_FACE",FACE,{"disambiguationData":[OSD([sQuery(id+"F4.wireOp",EDGE,"E35.filletArc")])]})])],"derivedFrom":makeQuery(id+"F5.opExtrude","CAP_EDGE",EDGE,{"disambiguationData":[OSD([subQ0])],"isStart":false})});}
            var Q4;
            {var subQ0=sQuery(id+"F0.wireOp",EDGE,"E25.7");var subQ1=sQuery(id+"F0.wireOp",EDGE,"E25.1");var subQ2=sQuery(id+"F0.wireOp",EDGE,"E25.6");var subQ3=sQuery(id+"F0.wireOp",EDGE,"E25.5");var subQ4=sQuery(id+"F0.wireOp",EDGE,"E25.4");var subQ5=sQuery(id+"F0.wireOp",EDGE,"E25.0");var subQ6=sQuery(id+"F0.wireOp",EDGE,"E25.2");var subQ7=sQuery(id+"F0.wireOp",EDGE,"E25.3");Q4=makeQuery(id+"F8.boolean.opBoolean","INTERSECT",EDGE,{"derivedFrom":[makeQuery(id+"F5.boolean.opBoolean","SPLIT",FACE,{"disambiguationData":[TD([makeQuery(id+"F2.opExtrude","SWEPT_FACE",FACE,{"disambiguationData":[OSD([subQ5])]})])],"derivedFrom":makeQuery(id+"F3.boolean.opBoolean","COPY",FACE,{"derivedFrom":makeQuery(id+"F3.opExtrude","CAP_FACE",FACE,{"disambiguationData":[OSD([subQ5,subQ1,subQ6,subQ7,subQ4,subQ3,subQ2,subQ0])],"isStart":false})})}),makeQuery(id+"F8.opExtrude","SWEPT_FACE",FACE,{"disambiguationData":[OSD([sQuery(id+"F7.wireOp",EDGE,"E67")])]})]});}
            var Q5;
            Q5=makeQuery(id+"F8.boolean.opBoolean","INTERSECT",EDGE,{"disambiguationData":[OD(0.0)],"derivedFrom":[makeQuery(id+"F5.opExtrude","SWEPT_FACE",FACE,{"disambiguationData":[OSD([sQuery(id+"F4.wireOp",EDGE,"E30")])]}),makeQuery(id+"F8.opExtrude","SWEPT_FACE",FACE,{"disambiguationData":[OSD([sQuery(id+"F7.wireOp",EDGE,"E67")])]})]});
            fillet(context, id + "F14", {"entities" : qUnion([Q0, Q1, Q2, Q3, Q4, Q5]), "radius" : 3 * mm, "tangentPropagation" : true, "allowEdgeOverflow" : false});
        }
        {
            var Q0;
            Q0=makeQuery(id+"F1.opExtrude","CAP_EDGE",EDGE,{"disambiguationData":[OSD([sQuery(id+"F0.wireOp",EDGE,"E1.bottom")])],"isStart":false});
            fillet(context, id + "F15", {"entities" : qUnion([Q0]), "radius" : 2 * mm, "tangentPropagation" : true, "allowEdgeOverflow" : false});
        }
        {
            var Q0;
            {var subQ0=sQuery(id+"F0.wireOp",EDGE,"E21.filletArc");var subQ1=sQuery(id+"F0.wireOp",EDGE,"E7");var subQ2=sQuery(id+"F0.wireOp",EDGE,"E6");var subQ3=sQuery(id+"F0.wireOp",EDGE,"E5");var subQ4=sQuery(id+"F0.wireOp",EDGE,"E4");var subQ5=sQuery(id+"F0.wireOp",EDGE,"E22.filletArc");var subQ6=sQuery(id+"F0.wireOp",EDGE,"E1.bottom");var subQ7=sQuery(id+"F0.wireOp",EDGE,"E1.right");var subQ8=sQuery(id+"F0.wireOp",EDGE,"E1.top");var subQ9=sQuery(id+"F0.wireOp",EDGE,"E1.left");var subQ10=sQuery(id+"F0.wireOp",EDGE,"E23.filletArc");var subQ11=sQuery(id+"F0.wireOp",EDGE,"E24.filletArc");Q0=makeQuery(id+"F2.boolean.opBoolean","SPLIT",FACE,{"disambiguationData":[TD([makeQuery(id+"F1.opExtrude","SWEPT_FACE",FACE,{"disambiguationData":[OSD([subQ6])]})])],"derivedFrom":makeQuery(id+"F1.opExtrude","CAP_FACE",FACE,{"disambiguationData":[OSD([subQ6,subQ8,subQ9,subQ7,subQ4,subQ3,subQ2,subQ1,subQ0,subQ5,subQ10,subQ11])],"isStart":true})});}
            var sketch = newSketch(context, id + "F16", { "sketchPlane" : qUnion([Q0])});
            skLineSegment(sketch, "E79.0.0", {"start": v(70, 90) * mm, "end": v(-70, 90) * mm});
            skArc(sketch, "E79.0.1", {"start": v(-70, 90) * mm, "mid": v(-77.07, 87.07) * mm, "end": v(-80, 80) * mm});
            skLineSegment(sketch, "E79.0.2", {"start": v(-80, 80) * mm, "end": v(-80, -80) * mm});
            skArc(sketch, "E79.0.3", {"start": v(-80, -80) * mm, "mid": v(-77.07, -87.07) * mm, "end": v(-70, -90) * mm});
            skLineSegment(sketch, "E79.0.4", {"start": v(-70, -90) * mm, "end": v(70, -90) * mm});
            skArc(sketch, "E79.0.5", {"start": v(70, -90) * mm, "mid": v(77.07, -87.07) * mm, "end": v(80, -80) * mm});
            skLineSegment(sketch, "E79.0.6", {"start": v(80, -80) * mm, "end": v(80, 80) * mm});
            skArc(sketch, "E79.0.7", {"start": v(80, 80) * mm, "mid": v(77.07, 87.07) * mm, "end": v(70, 90) * mm});
            skCircle(sketch, "E80.0", {"center": v(-60, 67.5) * mm, "radius": 4 * mm});
            skCircle(sketch, "E81.0", {"center": v(60, 67.5) * mm, "radius": 4 * mm});
            skCircle(sketch, "E82.0", {"center": v(60, -67.5) * mm, "radius": 4 * mm});
            skCircle(sketch, "E83.0", {"center": v(-60, -67.5) * mm, "radius": 4 * mm});
            skArc(sketch, "E84.0", {"start": v(-56.15, -48.18) * mm, "mid": v(0, -67.5) * mm, "end": v(56.15, -48.18) * mm});
            skArc(sketch, "E85.0", {"start": v(-60, -40.3) * mm, "mid": v(-58.99, -44.68) * mm, "end": v(-56.15, -48.18) * mm});
            skLineSegment(sketch, "E86.0", {"start": v(-60, 40.3) * mm, "end": v(-60, -40.3) * mm});
            skArc(sketch, "E87.0", {"start": v(-56.15, 48.18) * mm, "mid": v(-58.99, 44.68) * mm, "end": v(-60, 40.3) * mm});
            skArc(sketch, "E88.0", {"start": v(56.15, 48.18) * mm, "mid": v(0, 67.5) * mm, "end": v(-56.15, 48.18) * mm});
            skLineSegment(sketch, "E89.0", {"start": v(60, 40.3) * mm, "end": v(60, -40.3) * mm});
            skArc(sketch, "E90.0", {"start": v(60, 40.3) * mm, "mid": v(58.99, 44.68) * mm, "end": v(56.15, 48.18) * mm});
            skArc(sketch, "E91.0", {"start": v(56.15, -48.18) * mm, "mid": v(58.99, -44.68) * mm, "end": v(60, -40.3) * mm});
            skLineSegment(sketch, "E92", {"start": v(0, 90) * mm, "end": v(0, 120) * mm, "construction": true});
            skCircle(sketch, "E93", {"center": v(0, 120) * mm, "radius": 6 * mm});
            skArc(sketch, "E94", {"start": v(15, 120) * mm, "mid": v(0, 135) * mm, "end": v(-15, 120) * mm});
            skLineSegment(sketch, "E95", {"start": v(-15, 120) * mm, "end": v(-15, 108) * mm});
            skLineSegment(sketch, "E96", {"start": v(-15, 108) * mm, "end": v(-33, 90) * mm});
            skLineSegment(sketch, "E97", {"start": v(15, 108) * mm, "end": v(33, 90) * mm});
            skLineSegment(sketch, "E98", {"start": v(15, 120) * mm, "end": v(15, 108) * mm});
            skLineSegment(sketch, "E99", {"start": v(-80, 0) * mm, "end": v(80, 0) * mm, "construction": true});
            skLineSegment(sketch, "E100.MirrorCS", {"start": v(-15, -108) * mm, "end": v(-33, -90) * mm});
            skLineSegment(sketch, "E101.MirrorCS", {"start": v(-15, -120) * mm, "end": v(-15, -108) * mm});
            skArc(sketch, "E102.MirrorCS", {"start": v(15, -120) * mm, "mid": v(0, -135) * mm, "end": v(-15, -120) * mm});
            skCircle(sketch, "E103.MirrorC", {"center": v(0, -120) * mm, "radius": 6 * mm});
            skLineSegment(sketch, "E104.MirrorCS", {"start": v(0, -90) * mm, "end": v(0, -120) * mm, "construction": true});
            skLineSegment(sketch, "E105.MirrorCS", {"start": v(15, -120) * mm, "end": v(15, -108) * mm});
            skLineSegment(sketch, "E106.MirrorCS", {"start": v(15, -108) * mm, "end": v(33, -90) * mm});
            skSolve(sketch);
        }
        {
            var Q0;
            Q0=makeQuery(id+"F16.imprint","IMPRINT",FACE,{"disambiguationData":[TD([[makeQuery(id+"F16.imprint","IMPRINT",EDGE,{"derivedFrom":sQuery(id+"F16.wireOp",EDGE,"E93")}),-1.0]])]});
            var Q1;
            Q1=makeQuery(id+"F16.imprint","IMPRINT",FACE,{"disambiguationData":[TD([[makeQuery(id+"F16.imprint","IMPRINT",EDGE,{"derivedFrom":sQuery(id+"F16.wireOp",EDGE,"E80.0")}),-1.0]])]});
            var Q2;
            {var subQ0=sQuery(id+"F16.wireOp",EDGE,"E100.MirrorCS");Q2=makeQuery(id+"F16.imprint","IMPRINT",FACE,{"disambiguationData":[TD([[makeQuery(id+"F16.imprint","IMPRINT",EDGE,{"derivedFrom":subQ0}),-1.0]])]});}
            var Q3;
            Q3=makeQuery(id+"F2.opExtrude","CAP_FACE",FACE,{"disambiguationData":[OSD([sQuery(id+"F0.wireOp",EDGE,"E12"),sQuery(id+"F0.wireOp",EDGE,"E13"),sQuery(id+"F0.wireOp",EDGE,"E14"),sQuery(id+"F0.wireOp",EDGE,"E15"),sQuery(id+"F0.wireOp",EDGE,"E17.filletArc"),sQuery(id+"F0.wireOp",EDGE,"E18.filletArc"),sQuery(id+"F0.wireOp",EDGE,"E19.filletArc"),sQuery(id+"F0.wireOp",EDGE,"E20.filletArc"),sQuery(id+"F0.wireOp",EDGE,"E25.0"),sQuery(id+"F0.wireOp",EDGE,"E25.1"),sQuery(id+"F0.wireOp",EDGE,"E25.2"),sQuery(id+"F0.wireOp",EDGE,"E25.3"),sQuery(id+"F0.wireOp",EDGE,"E25.4"),sQuery(id+"F0.wireOp",EDGE,"E25.5"),sQuery(id+"F0.wireOp",EDGE,"E25.6"),sQuery(id+"F0.wireOp",EDGE,"E25.7")])],"isStart":false});
            extrude(context, id + "F17", {"entities" : qUnion([Q0, Q1, Q2]), "endBound" : BoundingType.UP_TO_SURFACE, "depth" : 25 * mm, "endBoundEntityFace" : qUnion([Q3]), "offsetDistance" : 25 * mm});
        }
    });
